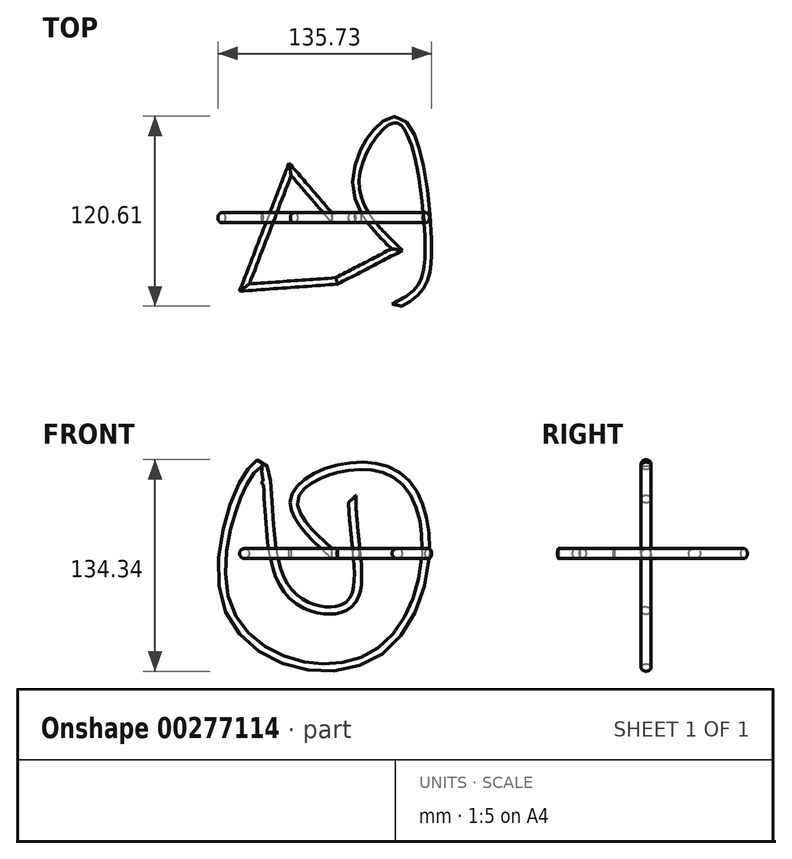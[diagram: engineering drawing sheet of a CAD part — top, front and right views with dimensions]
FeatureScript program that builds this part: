
annotation { "Feature Type Name" : "Feature", "Feature Type Description" : "" }
export const myFeature = defineFeature(function(context is Context, id is Id, definition is map)
    precondition{}
    {
        {
            var Q0;
            Q0=qCreatedBy(makeId("Top.planeOp"),FACE);
            var sketch = newSketch(context, id + "F0", { "sketchPlane" : qUnion([Q0])});
            skLineSegment(sketch, "E0", {"start": v(0, 0) * mm, "end": v(-26.51, 30.8) * mm});
            skLineSegment(sketch, "E1", {"start": v(-26.51, 30.8) * mm, "end": v(-55.5, -44.37) * mm});
            skLineSegment(sketch, "E2", {"start": v(-55.5, -44.37) * mm, "end": v(3.08, -40.15) * mm});
            skLineSegment(sketch, "E3", {"start": v(3.08, -40.15) * mm, "end": v(41.42, -20.22) * mm});
            skFitSpline(sketch, "E4", {"points": [v(41.42, -20.22) * mm, v(15.46, 25.07) * mm, v(41.42, 61.9) * mm, v(60.74, -4.82) * mm, v(56.22, -44.07) * mm, v(41.42, -55.54) * mm], "startDerivative": vector(-187.66, 182.97) * mm, "endDerivative": vector(-128.4, -70.87) * mm});
            skSolve(sketch);
        }
        {
            var Q0;
            Q0=qCreatedBy(makeId("Front.planeOp"),FACE);
            var sketch = newSketch(context, id + "F1", { "sketchPlane" : qUnion([Q0])});
            skFitSpline(sketch, "E5", {"points": [v(0, 0) * mm, v(-22.36, 38.26) * mm, v(43.77, 48.06) * mm, v(31.9, -60.97) * mm, v(-66.57, -32.83) * mm, v(-45.38, 56.73) * mm, v(-32.57, -15.96) * mm, v(3.02, -35.65) * mm, v(15.7, -23.46) * mm, v(12.93, 34.63) * mm], "startDerivative": vector(-467.8, 429.65) * mm, "endDerivative": vector(-13.3, 636.4) * mm});
            skSolve(sketch);
        }
        {
            var Q0;
            Q0=qCreatedBy(makeId("Right.planeOp"),FACE);
            var sketch = newSketch(context, id + "F2", { "sketchPlane" : qUnion([Q0])});
            skCircle(sketch, "E6", {"center": v(0, 0) * mm, "radius": 3.18 * mm});
            skSolve(sketch);
        }
        {
            var Q0;
            Q0=makeQuery(id+"F2.imprint","IMPRINT",FACE,{"disambiguationData":[TD([[makeQuery(id+"F2.imprint","IMPRINT",EDGE,{"derivedFrom":sQuery(id+"F2.wireOp",EDGE,"E6")}),1.0]])]});
            var Q1;
            Q1=sQuery(id+"F1.wireOp",EDGE,"E5");
            sweep(context, id + "F3", {"profiles" : qUnion([Q0]), "path" : qUnion([Q1])});
        }
        {
            var Q0;
            Q0=makeQuery(id+"F2.imprint","IMPRINT",FACE,{"disambiguationData":[TD([[makeQuery(id+"F2.imprint","IMPRINT",EDGE,{"derivedFrom":sQuery(id+"F2.wireOp",EDGE,"E6")}),1.0]])]});
            var Q1;
            Q1=sQuery(id+"F0.wireOp",EDGE,"E1");
            var Q2;
            Q2=sQuery(id+"F0.wireOp",EDGE,"E0");
            var Q3;
            Q3=sQuery(id+"F0.wireOp",EDGE,"E2");
            var Q4;
            Q4=sQuery(id+"F0.wireOp",EDGE,"E3");
            var Q5;
            Q5=sQuery(id+"F0.wireOp",EDGE,"E4");
            sweep(context, id + "F4", {"profiles" : qUnion([Q0]), "path" : qUnion([Q1, Q2, Q3, Q4, Q5])});
        }
    });
